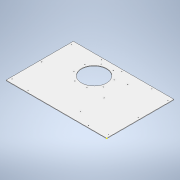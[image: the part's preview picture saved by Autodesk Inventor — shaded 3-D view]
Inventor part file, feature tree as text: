
AUTODESK INVENTOR PART (.ipt)
format: ipt  version: 2020 (Build 240168000, 168)  size: 187,392 bytes
history: native  units: mm
features: sketch x9, hole x6, extrude x2, pattern_circular x1
ambient origin geometry x8: Origin, YZ Plane, XZ Plane, XY Plane, X Axis, Y Axis, Z Axis, Center Point
bodies: Solid1 (feature_tree)
feature tree (18):
  extrude  "Extrusion1"  Depth=669.0mm
  extrude  "Extrusion2"  Depth=5.0mm
  hole  "Hole1"  [1 undecoded]
  sketch  "Sketch5"  dims[d7=0.0mm d8=0.0mm d9=20.0mm d11=40.0mm]
  hole  "Hole3"  [1 undecoded]
  pattern_circular  "Circular Pattern1"  Count=4  [1 undecoded]
  hole  "Hole4"  [1 undecoded]
  hole  "Hole5"  [1 undecoded]
  hole  "Hole6"  [1 undecoded]
  hole  "Hole7"  [1 undecoded]
  sketch  "Sketch1"  dims[d0=1000.0mm d1=669.0mm]
  sketch  "Sketch2"  dims[d2=5.0mm d3=0.0mm d4=250.0mm]
  sketch  "Sketch3"  dims[d5=475.0mm d6=600.0mm]
  sketch  "Sketch6"  dims[d12=334.5mm d13=20.0mm]
  sketch  "Sketch7"  dims[d14=40.0mm d15=20.0mm]
  sketch  "Sketch8"  dims[d16=40.0mm d17=20.0mm]
  sketch  "Sketch9"  dims[d18=334.5mm d19=20.0mm]
  sketch  "Sketch10"  dims[d20=20.0mm d21=40.0mm d22=5.5mm d23=6.0mm d24=11.5mm d25=2.0mm d26=90.0deg d27=8.0mm d28=20.594885mm d40=5.5mm d41=16.0mm d42=10.0mm d43=2.0mm d44=90.0deg d45=22.2mm d46=20.594885mm d48=650.0mm d49=150.0mm d50=80.0mm d51=360.0deg d54=19.5mm d55=700.0mm d56=800.0mm d61=5.5mm d62=16.0mm d63=10.0mm d64=2.0mm d65=90.0deg d66=22.2mm d67=20.594885mm d68=19.5mm d73=5.5mm d74=16.0mm d75=10.0mm d76=2.0mm d77=90.0deg d78=8.0mm d79=20.594885mm d80=19.5mm d81=200.0mm d82=200.0mm d83=19.5mm d84=500.0mm d85=19.5mm d86=5.5mm d87=6.0mm d88=4.0mm d89=2.0mm d90=90.0deg d91=8.0mm d92=20.594885mm d93=100.0mm d94=334.5mm d95=100.0mm d96=5.5mm d97=6.0mm d98=4.0mm d99=2.0mm d100=90.0deg d101=8.0mm d102=20.594885mm d103=360.0mm d104=360.0mm d105=360.0mm]
note: 7 required parameter values undecoded (feature->parameter linkage not recoverable at this tier; creation-order binding heuristic only, values carry confidence <= 0.55)
